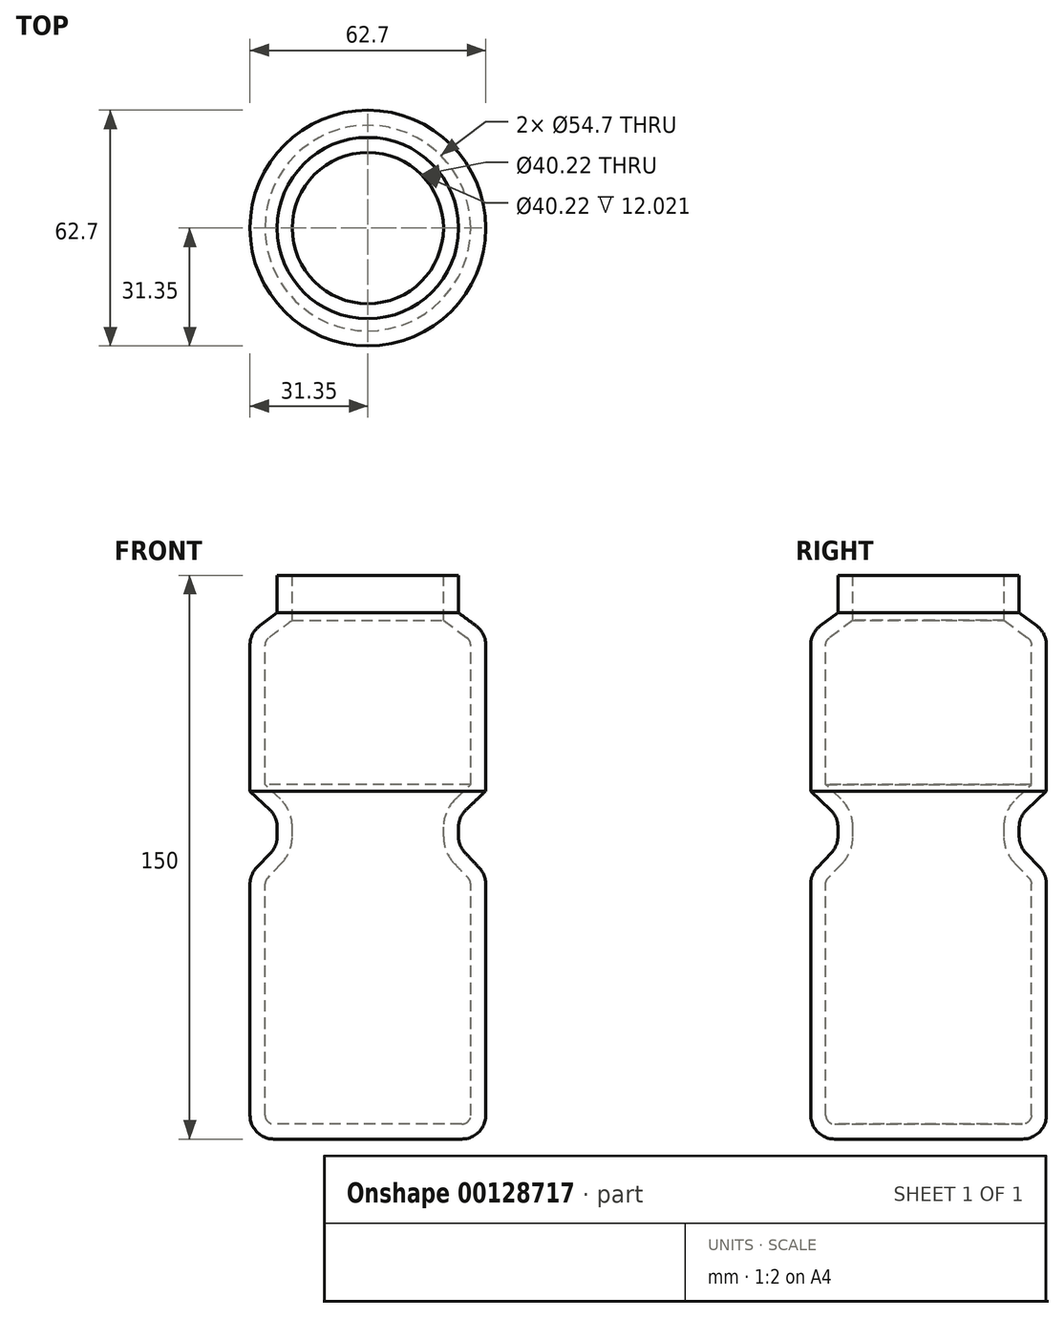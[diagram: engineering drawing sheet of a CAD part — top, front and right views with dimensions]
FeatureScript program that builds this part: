
annotation { "Feature Type Name" : "Feature", "Feature Type Description" : "" }
export const myFeature = defineFeature(function(context is Context, id is Id, definition is map)
    precondition{}
    {
        {
            var Q0;
            Q0=qCreatedBy(makeId("Front.planeOp"),FACE);
            var sketch = newSketch(context, id + "F0", { "sketchPlane" : qUnion([Q0])});
            skLineSegment(sketch, "E0", {"start": v(0, 0) * mm, "end": v(25, 0) * mm});
            skLineSegment(sketch, "E1", {"start": v(31.35, 6.35) * mm, "end": v(31.35, 67.84) * mm});
            skLineSegment(sketch, "E2", {"start": v(29.6, 72.21) * mm, "end": v(25.86, 76.14) * mm});
            skLineSegment(sketch, "E3", {"start": v(24.1, 80.52) * mm, "end": v(24.1, 82.97) * mm});
            skPoint(sketch, "E4.endSnap0", {"position": v(27.73, 74.18) * mm});
            skLineSegment(sketch, "E5", {"start": v(26.08, 87.57) * mm, "end": v(31.35, 92.59) * mm});
            skLineSegment(sketch, "E6", {"start": v(31.35, 92.59) * mm, "end": v(31.35, 131.46) * mm});
            skLineSegment(sketch, "E7", {"start": v(28.77, 136.57) * mm, "end": v(24.1, 140) * mm});
            skLineSegment(sketch, "E8", {"start": v(24.1, 140) * mm, "end": v(24.1, 150) * mm});
            skLineSegment(sketch, "E9", {"start": v(24.1, 150) * mm, "end": v(0, 150) * mm});
            skPoint(sketch, "E10.visualSharp", {"position": v(31.35, 0) * mm});
            skArc(sketch, "E10.filletArc", {"start": v(25, 0) * mm, "mid": v(29.5, 1.86) * mm, "end": v(31.35, 6.35) * mm});
            skPoint(sketch, "E11.visualSharp", {"position": v(31.35, 70.38) * mm});
            skArc(sketch, "E11.filletArc", {"start": v(31.35, 67.84) * mm, "mid": v(30.9, 70.2) * mm, "end": v(29.6, 72.21) * mm});
            skPoint(sketch, "E12.visualSharp", {"position": v(24.1, 77.98) * mm});
            skArc(sketch, "E12.filletArc", {"start": v(24.1, 80.52) * mm, "mid": v(24.56, 78.16) * mm, "end": v(25.86, 76.14) * mm});
            skPoint(sketch, "E13.visualSharp", {"position": v(24.1, 85.69) * mm});
            skArc(sketch, "E13.filletArc", {"start": v(26.08, 87.57) * mm, "mid": v(24.62, 85.47) * mm, "end": v(24.1, 82.97) * mm});
            skPoint(sketch, "E14.visualSharp", {"position": v(31.35, 134.66) * mm});
            skArc(sketch, "E14.filletArc", {"start": v(31.35, 131.46) * mm, "mid": v(30.67, 134.32) * mm, "end": v(28.77, 136.57) * mm});
            skLineSegment(sketch, "E15", {"start": v(0, 150) * mm, "end": v(0, 0) * mm});
            skSolve(sketch);
        }
        {
            var Q0;
            Q0=makeQuery(id+"F0.imprint","IMPRINT",FACE,{"disambiguationData":[TD([[makeQuery(id+"F0.imprint","IMPRINT",EDGE,{"derivedFrom":sQuery(id+"F0.wireOp",EDGE,"E0")}),1.0]])]});
            var Q1;
            Q1=sQuery(id+"F0.wireOp",EDGE,"E15");
            revolve(context, id + "F1", {"entities" : qUnion([Q0]), "axis" : qUnion([Q1]), "revolveType" : RevolveType.FULL});
        }
        {
            var Q0;
            Q0=makeQuery(id+"F1.opRevolve","SWEPT_FACE",FACE,{"disambiguationData":[OSD([sQuery(id+"F0.wireOp",EDGE,"E9")])]});
            shell(context, id + "F2", {"entities" : qUnion([Q0]), "thickness" : 4 * mm});
        }
    });
